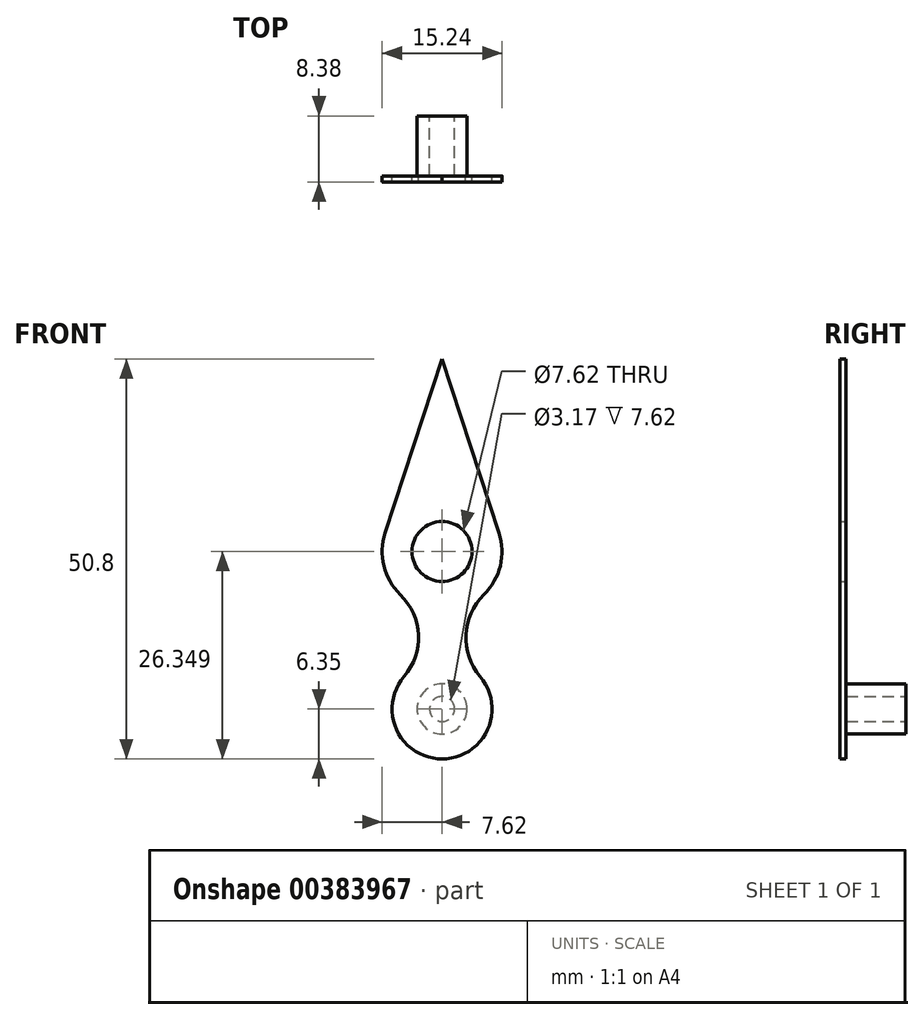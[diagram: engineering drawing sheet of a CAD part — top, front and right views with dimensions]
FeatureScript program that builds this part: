
annotation { "Feature Type Name" : "Feature", "Feature Type Description" : "" }
export const myFeature = defineFeature(function(context is Context, id is Id, definition is map)
    precondition{}
    {
        {
            var Q0;
            Q0=qCreatedBy(makeId("Front.planeOp"),FACE);
            var sketch = newSketch(context, id + "F0", { "sketchPlane" : qUnion([Q0])});
            skLineSegment(sketch, "E0", {"start": v(0, 0) * mm, "end": v(0, 50.8) * mm});
            skArc(sketch, "E1", {"start": v(-4.83, 10.47) * mm, "mid": v(0, 0) * mm, "end": v(4.83, 10.47) * mm});
            skArc(sketch, "E2", {"start": v(-7.24, 28.72) * mm, "mid": v(-7.4, 24.53) * mm, "end": v(-5.31, 20.89) * mm});
            skCircle(sketch, "E3", {"center": v(0, 26.35) * mm, "radius": 3.81 * mm});
            skLineSegment(sketch, "E4", {"start": v(0, 50.8) * mm, "end": v(-7.24, 28.72) * mm});
            skLineSegment(sketch, "E5", {"start": v(0, 50.8) * mm, "end": v(7.24, 28.72) * mm});
            skArc(sketch, "E6", {"start": v(-4.83, 10.47) * mm, "mid": v(-3.01, 15.78) * mm, "end": v(-5.31, 20.89) * mm});
            skArc(sketch, "E7", {"start": v(5.31, 20.89) * mm, "mid": v(3.01, 15.78) * mm, "end": v(4.83, 10.47) * mm});
            skArc(sketch, "E8.trimOffspring", {"start": v(5.31, 20.89) * mm, "mid": v(7.4, 24.53) * mm, "end": v(7.24, 28.72) * mm});
            skSolve(sketch);
        }
        {
            var Q0;
            {var subQ7=sQuery(id+"F0.wireOp",EDGE,"E5");Q0=makeQuery(id+"F0.imprint","IMPRINT",FACE,{"disambiguationData":[TD([[makeQuery(id+"F0.imprint","IMPRINT",EDGE,{"derivedFrom":subQ7}),-1.0]])]});}
            var Q1;
            Q1=makeQuery(id+"F0.imprint","IMPRINT",FACE,{"disambiguationData":[TD([[makeQuery(id+"F0.imprint","IMPRINT",EDGE,{"derivedFrom":sQuery(id+"F0.wireOp",EDGE,"E2")}),1.0]])]});
            extrude(context, id + "F1", {"entities" : qUnion([Q0, Q1]), "endBound" : BoundingType.SYMMETRIC, "depth" : 0.76 * mm});
        }
        {
            var Q0;
            Q0=makeQuery(id+"F1.opExtrude","CAP_FACE",FACE,{"disambiguationData":[OSD([sQuery(id+"F0.wireOp",EDGE,"E1"),sQuery(id+"F0.wireOp",EDGE,"E2"),sQuery(id+"F0.wireOp",EDGE,"E3"),sQuery(id+"F0.wireOp",EDGE,"E4"),sQuery(id+"F0.wireOp",EDGE,"E5"),sQuery(id+"F0.wireOp",EDGE,"E6"),sQuery(id+"F0.wireOp",EDGE,"E7"),sQuery(id+"F0.wireOp",EDGE,"E8.trimOffspring")])],"isStart":true});
            var sketch = newSketch(context, id + "F2", { "sketchPlane" : qUnion([Q0])});
            skCircle(sketch, "E9", {"center": v(0, 6.35) * mm, "radius": 3.18 * mm});
            skSolve(sketch);
        }
        {
            var Q0;
            Q0=makeQuery(id+"F2.imprint","IMPRINT",FACE,{"disambiguationData":[TD([[makeQuery(id+"F2.imprint","IMPRINT",EDGE,{"derivedFrom":sQuery(id+"F2.wireOp",EDGE,"E9")}),1.0]])]});
            extrude(context, id + "F3", {"entities" : qUnion([Q0]), "operationType" : NewBodyOperationType.ADD, "depth" : 7.62 * mm});
        }
        {
            var Q0;
            Q0=makeQuery(id+"F3.opExtrude","CAP_FACE",FACE,{"disambiguationData":[OSD([sQuery(id+"F2.wireOp",EDGE,"E9")])],"isStart":false});
            var sketch = newSketch(context, id + "F4", { "sketchPlane" : qUnion([Q0])});
            skCircle(sketch, "E10", {"center": v(0, 6.35) * mm, "radius": 1.59 * mm});
            skSolve(sketch);
        }
        {
            var Q0;
            Q0=makeQuery(id+"F4.imprint","IMPRINT",FACE,{"disambiguationData":[TD([[makeQuery(id+"F4.imprint","IMPRINT",EDGE,{"derivedFrom":sQuery(id+"F4.wireOp",EDGE,"E10")}),1.0]])]});
            extrude(context, id + "F5", {"entities" : qUnion([Q0]), "operationType" : NewBodyOperationType.REMOVE, "oppositeDirection" : true, "depth" : 7.62 * mm});
        }
    });
